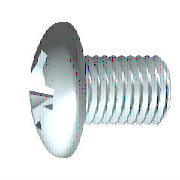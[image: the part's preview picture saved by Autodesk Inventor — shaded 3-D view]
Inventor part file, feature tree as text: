
AUTODESK INVENTOR PART (.ipt)
format: ipt  version: 2023.3 (Build 273359000, 359)  size: 336,896 bytes
history: native  units: mm (DEFAULTED — no unit token found)
features: other x3, extrude x2, plane x1
ambient origin geometry x7: Origin, YZ Plane, XZ Plane, X Axis, Y Axis, Z Axis, Center Point
bodies: Solid1 (feature_tree)
feature tree (6):
  other  "Körper"
  other  "IDS_WORKPLANE{1}"
  extrude  "Loch"  Depth=3.0mm
  other  "Schnitt"
  extrude  "Sternförmiger Schnitt"  Depth=1.75mm
  plane  "Work Plane3"
